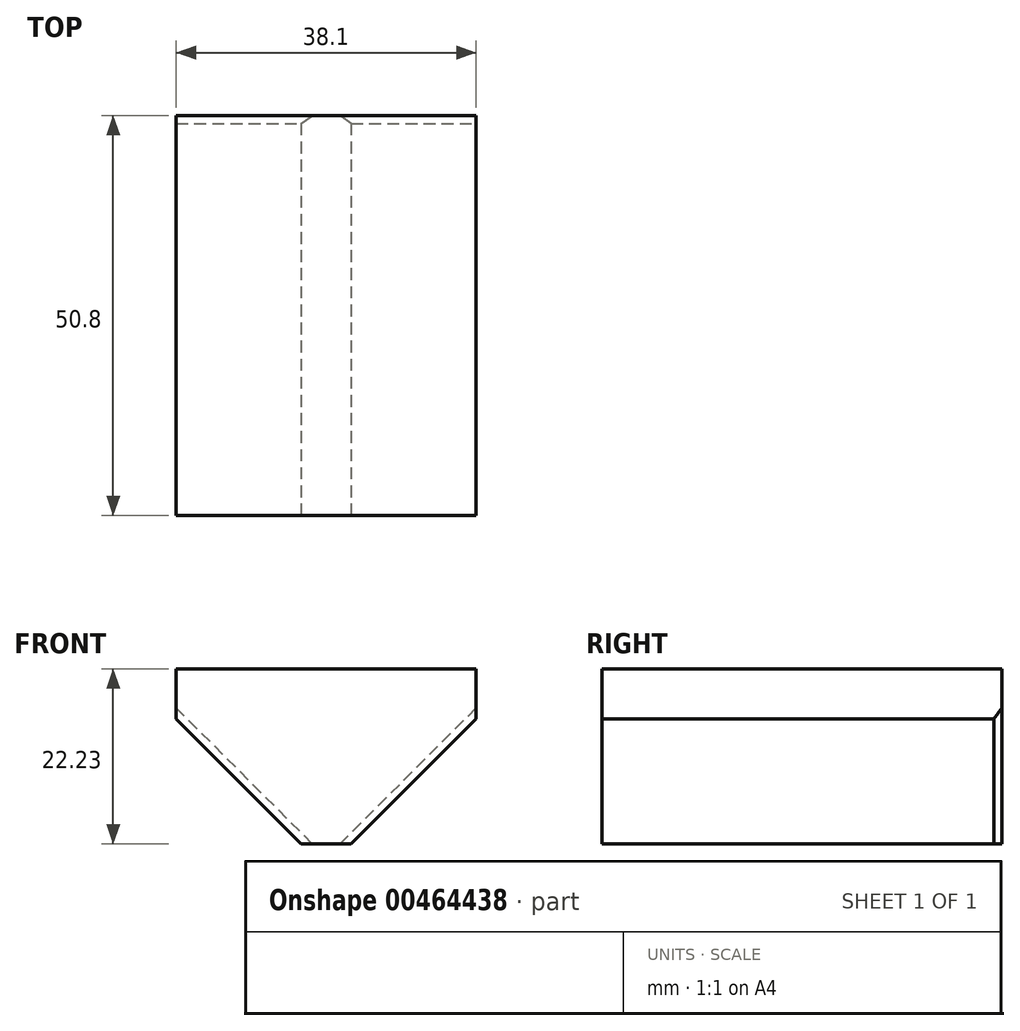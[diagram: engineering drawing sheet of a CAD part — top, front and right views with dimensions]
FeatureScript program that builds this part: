
annotation { "Feature Type Name" : "Feature", "Feature Type Description" : "" }
export const myFeature = defineFeature(function(context is Context, id is Id, definition is map)
    precondition{}
    {
        {
            var Q0;
            Q0=qCreatedBy(makeId("Top.planeOp"),FACE);
            var sketch = newSketch(context, id + "F0", { "sketchPlane" : qUnion([Q0])});
            skLineSegment(sketch, "E0.bottom", {"start": v(0, 0) * mm, "end": v(38.1, 0) * mm});
            skLineSegment(sketch, "E0.top", {"start": v(0, 50.8) * mm, "end": v(38.1, 50.8) * mm});
            skLineSegment(sketch, "E0.left", {"start": v(0, 0) * mm, "end": v(0, 50.8) * mm});
            skLineSegment(sketch, "E0.right", {"start": v(38.1, 0) * mm, "end": v(38.1, 50.8) * mm});
            skSolve(sketch);
        }
        {
            var Q0;
            Q0 = qSketchRegion(id + "F0", true);
            extrude(context, id + "F1", {"entities" : qUnion([Q0]), "depth" : 22.22 * mm});
        }
        {
            var Q0;
            Q0=makeQuery(id+"F1.opExtrude","SWEPT_FACE",FACE,{"disambiguationData":[OSD([sQuery(id+"F0.wireOp",EDGE,"E0.bottom")])]});
            var sketch = newSketch(context, id + "F2", { "sketchPlane" : qUnion([Q0])});
            skLineSegment(sketch, "E1", {"start": v(22.23, 0) * mm, "end": v(38.1, 15.88) * mm});
            skLineSegment(sketch, "E2", {"start": v(15.88, 0) * mm, "end": v(0, 15.88) * mm});
            skLineSegment(sketch, "E3", {"start": v(38.1, 15.88) * mm, "end": v(38.1, 0) * mm});
            skLineSegment(sketch, "E4", {"start": v(38.1, 0) * mm, "end": v(22.23, 0) * mm});
            skLineSegment(sketch, "E5", {"start": v(0, 15.88) * mm, "end": v(0, 0) * mm});
            skLineSegment(sketch, "E6", {"start": v(0, 0) * mm, "end": v(15.88, 0) * mm});
            skSolve(sketch);
        }
        {
            var Q0;
            Q0 = qSketchRegion(id + "F2", true);
            extrude(context, id + "F3", {"entities" : qUnion([Q0]), "operationType" : NewBodyOperationType.REMOVE, "endBound" : BoundingType.THROUGH_ALL, "oppositeDirection" : true, "depth" : 25.4 * mm});
        }
        {
            var Q0;
            Q0=makeQuery(id+"F3.boolean.opBoolean","COPY",EDGE,{"derivedFrom":makeQuery(id+"F3.opExtrude","CAP_EDGE",EDGE,{"disambiguationData":[OSD([sQuery(id+"F2.wireOp",EDGE,"E1")])],"isStart":true})});
            var Q1;
            Q1=makeQuery(id+"F3.boolean.opBoolean","COPY",EDGE,{"derivedFrom":makeQuery(id+"F3.opExtrude","CAP_EDGE",EDGE,{"disambiguationData":[OSD([sQuery(id+"F2.wireOp",EDGE,"E2")])],"isStart":true})});
            var Q2;
            Q2=makeQuery(id+"F3.boolean.opBoolean","INTERSECT",EDGE,{"derivedFrom":[makeQuery(id+"F1.opExtrude","SWEPT_FACE",FACE,{"disambiguationData":[OSD([sQuery(id+"F0.wireOp",EDGE,"E0.top")])]}),makeQuery(id+"F3.opExtrude","SWEPT_FACE",FACE,{"disambiguationData":[OSD([sQuery(id+"F2.wireOp",EDGE,"E1")])]})]});
            var Q3;
            Q3=makeQuery(id+"F3.boolean.opBoolean","INTERSECT",EDGE,{"derivedFrom":[makeQuery(id+"F1.opExtrude","SWEPT_FACE",FACE,{"disambiguationData":[OSD([sQuery(id+"F0.wireOp",EDGE,"E0.top")])]}),makeQuery(id+"F3.opExtrude","SWEPT_FACE",FACE,{"disambiguationData":[OSD([sQuery(id+"F2.wireOp",EDGE,"E2")])]})]});
            chamfer(context, id + "F4", {"entities" : qUnion([Q0, Q1, Q2, Q3]), "width" : 1 * mm, "tangentPropagation" : true});
        }
    });
